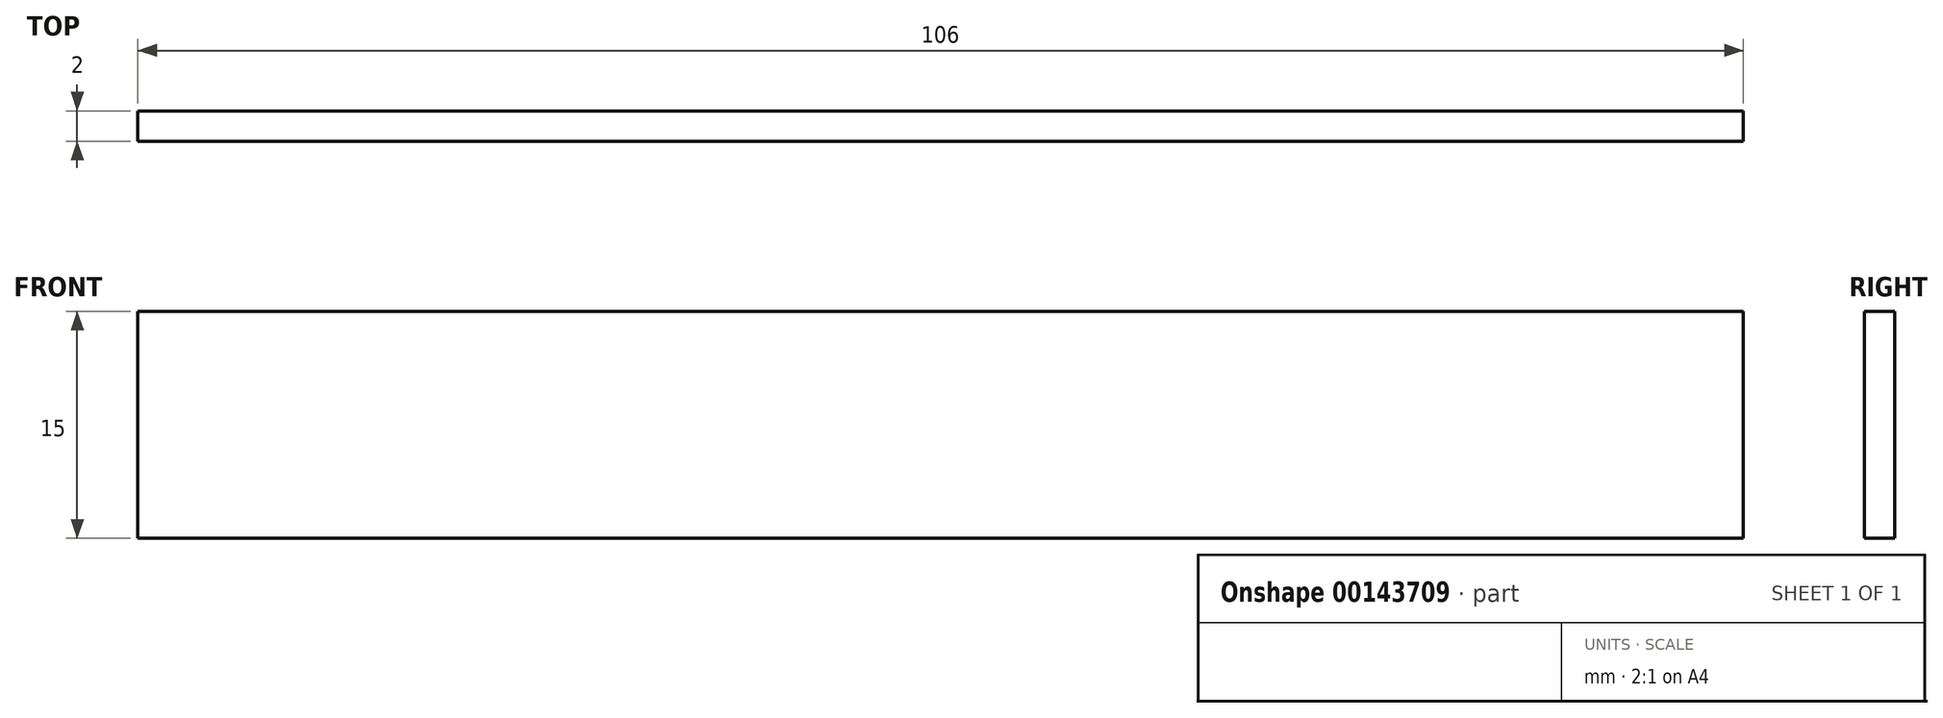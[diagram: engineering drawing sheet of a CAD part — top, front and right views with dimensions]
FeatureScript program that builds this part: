
annotation { "Feature Type Name" : "Feature", "Feature Type Description" : "" }
export const myFeature = defineFeature(function(context is Context, id is Id, definition is map)
    precondition{}
    {
        {
            var Q0;
            Q0=qCreatedBy(makeId("Front.planeOp"),FACE);
            var sketch = newSketch(context, id + "F0", { "sketchPlane" : qUnion([Q0])});
            skLineSegment(sketch, "E0.bottom", {"start": v(53, -7.5) * mm, "end": v(-53, -7.5) * mm});
            skLineSegment(sketch, "E0.top", {"start": v(53, 7.5) * mm, "end": v(-53, 7.5) * mm});
            skLineSegment(sketch, "E0.left", {"start": v(53, -7.5) * mm, "end": v(53, 7.5) * mm});
            skLineSegment(sketch, "E0.right", {"start": v(-53, -7.5) * mm, "end": v(-53, 7.5) * mm});
            skPoint(sketch, "E0.middle", {"position": v(0, 0) * mm});
            skSolve(sketch);
        }
        {
            var Q0;
            Q0 = qSketchRegion(id + "F0", true);
            extrude(context, id + "F1", {"entities" : qUnion([Q0]), "depth" : 2 * mm});
        }
    });
